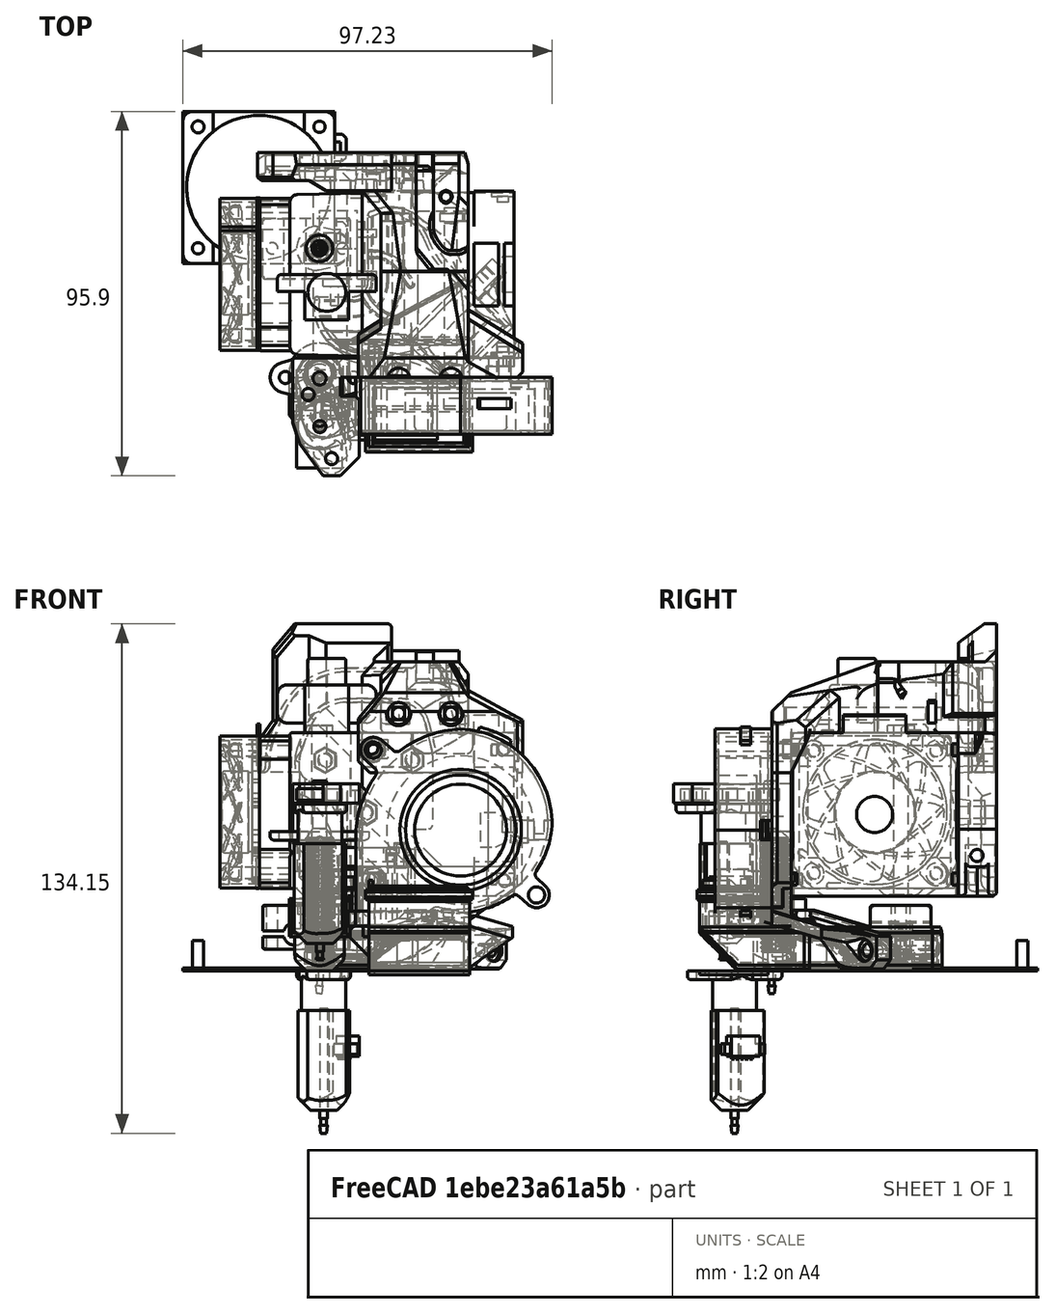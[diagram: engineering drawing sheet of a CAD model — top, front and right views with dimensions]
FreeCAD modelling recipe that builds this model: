
FCSTD DOCUMENT  (FreeCAD 0.18R16146 (Git))
Label: bearmera-5015-rev-1
License: All rights reserved
LicenseURL: http://en.wikipedia.org/wiki/All_rights_reserved
objects: Part::Box×73, Part::Cut×52, Part::Feature×47, Part::MultiFuse×32, Part::Cylinder×31, Part::Chamfer×27, Sketcher::SketchObject×6, PartDesign::Body×4, App::DocumentObjectGroup×3, Part::MultiCommon×3, Mesh::Feature×2, PartDesign::AdditiveLoft×2, PartDesign::Pad×2, App::Part×1
note: 283 computed .brp shape members not serialized (recipe doc carries the construction recipe); baked Part::Feature solids carry a one-line shape summary decoded from their .brp

FEATURE [Part::Feature] Part__Feature018  label="NOZZLE-POS"
  Placement = pos=(-0.025,3.1e-14,12.45) rot=(0.707107,0.707107,0;3.14159rad)
  shape: bbox 8.083 x 7 x 12.5 mm, 18 faces (baked)
FEATURE [Part::Feature] Part__Feature017  label="v6_heaterblock v1"
  Placement = pos=(-14.9885,-8.00025,5.758) rot=(0,0,1;0rad)
  shape: bbox 23 x 16 x 11.5 mm, 37 faces (baked)
FEATURE [Part::Feature] Part__Feature013  label="stepper"
  Placement = pos=(51.225,-28.9,19.7) rot=(0,0,1;1.5708rad)
  shape: bbox 40 x 44 x 47.7 mm, 101 faces (baked)
FEATURE [Part::Feature] Part__Feature014  label="heatsink"
  Placement = pos=(11.225,-28.4,19.7) rot=(0,0,1;1.5708rad)
  shape: bbox 30.92 x 43.26 x 62.61 mm, 110 faces (baked)
FEATURE [Part::Feature] Part__Feature016  label="e3d_hemera_fan v1"
  Placement = pos=(-15.775,13.2,61.8) rot=(0.57735,-0.57735,0.57735;4.18879rad)
  shape: bbox 10.51 x 40.01 x 40.01 mm, 129 faces (baked)
FEATURE [Mesh::Feature] lower_4020_fan_duct  label="lower_4020-fan-duct"
  Placement = pos=(11.3,-33.9,19.8) rot=(0,0,1;0rad)
FEATURE [Part::Feature] Cut007002001001  label="fan-mount-frame001"
  shape: bbox 28.2 x 19.2 x 3.5 mm, 16 faces (baked)
FEATURE [Part::Feature] Part__Feature  label="duct001"
  Placement = pos=(13,-15,0) rot=(0,0,1;0rad)
  shape: bbox 62.87 x 53.67 x 16.75 mm, 145 faces (baked)
FEATURE [Part::Feature] Part__Feature025  label="duct002"
  Placement = pos=(13,-15,0) rot=(0,0,1;0rad)
  shape: bbox 62.87 x 53.67 x 16.75 mm, 145 faces (baked)
FEATURE [Part::Box] Box  label="Cube"
  AttacherType = Attacher::AttachEngine3D
  Height = 17
  Length = 29
  Placement = pos=(26,-38,0) rot=(0,0,1;0rad)
  Width = 48
FEATURE [Part::Box] Box001  label="Cube001"
  AttacherType = Attacher::AttachEngine3D
  Height = 27
  Length = 26
  Placement = pos=(0,-34,0) rot=(0,0,1;0rad)
  Width = 10
FEATURE [Part::Cut] Cut
  Base = -> Part__Feature
  Tool = -> Box
FEATURE [Part::Cut] Cut007002001002
  Base = -> Cut
  Placement = pos=(0,0,-0.45) rot=(0,0,1;0rad)
  Tool = -> Box001
FEATURE [Part::Box] Box002  label="Cube002"
  AttacherType = Attacher::AttachEngine3D
  Height = 2
  Length = 13
  Placement = pos=(13,-24,0.8) rot=(0,0,1;0rad)
  Width = 4
FEATURE [Part::Box] Box003  label="Cube003"
  AttacherType = Attacher::AttachEngine3D
  Height = 1
  Length = 5
  Placement = pos=(21,-24,0.8) rot=(0,0,1;0rad)
  Width = 13
FEATURE [Part::Cut] Cut007002001003
  Base = -> Cut007002001002
  Tool = -> Box002
FEATURE [Part::Cut] Cut007002001004
  Base = -> Cut007002001003
  Tool = -> Box003
FEATURE [Part::Box] Box004  label="Cube004"
  AttacherType = Attacher::AttachEngine3D
  Height = 10
  Length = 24
  Placement = pos=(7,-30,10) rot=(0,0,1;0rad)
  Width = 27
FEATURE [Part::Cut] Cut007002001005
  Base = -> Cut007002001004
  Tool = -> Box004
FEATURE [Part::Box] Box005  label="Cube005"
  AttacherType = Attacher::AttachEngine3D
  Height = 10
  Length = 32
  Placement = pos=(-2,-38,0) rot=(0,0,1;0rad)
  Width = 14
FEATURE [Part::Box] Box007  label="Cube007"
  AttacherType = Attacher::AttachEngine3D
  Height = 10
  Length = 21
  Placement = pos=(26,-24,0) rot=(0,0,1;0rad)
  Width = 21
FEATURE [Part::Box] Box008  label="Cube008"
  AttacherType = Attacher::AttachEngine3D
  Height = 1
  Length = 41
  Placement = pos=(10,-35,9) rot=(0,0,1;0.506145rad)
  Width = 10
FEATURE [Part::MultiFuse] Fusion
  Shapes = -> [Cut007002001005,Box008]
FEATURE [Part::Cut] Cut007002001006
  Base = -> Fusion
  Tool = -> Box005
FEATURE [Part::Cut] Cut007002001007  label="duct-square-cut"
  Base = -> Cut007002001006
  Tool = -> Box007
FEATURE [Part::Feature] Cut007002001007001  label="Cut007002001008"
  Placement = pos=(0,0,1.5) rot=(0,0,1;0rad)
  shape: bbox 41.3 x 51.61 x 10 mm, 88 faces (baked)
FEATURE [Part::Box] Box012  label="Cube012"
  AttacherType = Attacher::AttachEngine3D
  Height = 1
  Length = 26.5
  Placement = pos=(13,-53,0) rot=(0,0,1;0rad)
  Width = 18
FEATURE [Part::Box] Box013  label="Cube013"
  AttacherType = Attacher::AttachEngine3D
  Height = 1
  Length = 23.5
  Placement = pos=(14.5,-51.5,0) rot=(0,0,1;0rad)
  Width = 15
FEATURE [Part::Cut] Cut007002001007002
  Base = -> Box012
  Placement = pos=(0,0,-1) rot=(0,0,1;0rad)
  Tool = -> Box013
FEATURE [Sketcher::SketchObject] Sketch
  AttachmentOffset = pos=(0,0,19) rot=(0,0,1;0rad)
  MapMode = 5
  Placement = pos=(0,0,19) rot=(0,0,1;0rad)
  Support = -> [XY_Plane]
  sketch-geometry (8):
    g0: LineSegment StartX=13 StartY=-35 StartZ=0 EndX=39.5 EndY=-35 EndZ=0
    g1: LineSegment StartX=39.5 StartY=-35 StartZ=0 EndX=39.5 EndY=-53 EndZ=0
    g2: LineSegment StartX=39.5 StartY=-53 StartZ=0 EndX=13 EndY=-53 EndZ=0
    g3: LineSegment StartX=13 StartY=-53 StartZ=0 EndX=13 EndY=-35 EndZ=0
    g4: LineSegment StartX=14.5 StartY=-36.5 StartZ=0 EndX=38 EndY=-36.5 EndZ=0
    g5: LineSegment StartX=38 StartY=-36.5 StartZ=0 EndX=38 EndY=-51.5 EndZ=0
    g6: LineSegment StartX=38 StartY=-51.5 StartZ=0 EndX=14.5 EndY=-51.5 EndZ=0
    g7: LineSegment StartX=14.5 StartY=-51.5 StartZ=0 EndX=14.5 EndY=-36.5 EndZ=0
  constraints (16):
    c: Coincident(g0,g1)
    c: Coincident(g1,g2)
    c: Coincident(g2,g3)
    c: Coincident(g3,g0)
    c: Horizontal(g0)
    c: Horizontal(g2)
    c: Vertical(g1)
    c: Vertical(g3)
    c: Coincident(g4,g5)
    c: Coincident(g5,g6)
    c: Coincident(g6,g7)
    c: Coincident(g7,g4)
    c: Horizontal(g4)
    c: Horizontal(g6)
    c: Vertical(g5)
    c: Vertical(g7)
FEATURE [Sketcher::SketchObject] Sketch001
  AttachmentOffset = pos=(0,0,10.45) rot=(0,0,1;0rad)
  MapMode = 5
  Placement = pos=(0,0,10.45) rot=(0,0,1;0rad)
  Support = -> [XY_Plane]
  sketch-geometry (8):
    g0: LineSegment StartX=13 StartY=-53 StartZ=0 EndX=39.5 EndY=-53 EndZ=0
    g1: LineSegment StartX=39.5 StartY=-53 StartZ=0 EndX=39.5 EndY=-24 EndZ=0
    g2: LineSegment StartX=39.5 StartY=-24 StartZ=0 EndX=13 EndY=-24 EndZ=0
    g3: LineSegment StartX=13 StartY=-24 StartZ=0 EndX=13 EndY=-53 EndZ=0
    g4: LineSegment StartX=38 StartY=-25.5 StartZ=0 EndX=14.5 EndY=-25.5 EndZ=0
    g5: LineSegment StartX=14.5 StartY=-25.5 StartZ=0 EndX=14.5 EndY=-51.5 EndZ=0
    g6: LineSegment StartX=14.5 StartY=-51.5 StartZ=0 EndX=38 EndY=-51.5 EndZ=0
    g7: LineSegment StartX=38 StartY=-51.5 StartZ=0 EndX=38 EndY=-25.5 EndZ=0
  constraints (16):
    c: Coincident(g0,g1)
    c: Coincident(g1,g2)
    c: Coincident(g2,g3)
    c: Coincident(g3,g0)
    c: Horizontal(g0)
    c: Horizontal(g2)
    c: Vertical(g1)
    c: Vertical(g3)
    c: Coincident(g4,g5)
    c: Coincident(g5,g6)
    c: Coincident(g6,g7)
    c: Coincident(g7,g4)
    c: Horizontal(g4)
    c: Horizontal(g6)
    c: Vertical(g5)
    c: Vertical(g7)
FEATURE [PartDesign::AdditiveLoft] AdditiveLoft
  Closed = false
  Profile = -> Sketch
  Ruled = false
  Sections = -> [Sketch001]
FEATURE [PartDesign::Body] Body  label="ramp"
  Group = -> [Sketch,Sketch001,AdditiveLoft]
  Origin = -> Origin
  Tip = -> AdditiveLoft
FEATURE [Part::Feature] Body001  label="ramp001"
  Placement = pos=(0,0,-0.45) rot=(0,0,1;0rad)
  shape: bbox 26.5 x 29 x 8.55 mm, 10 faces (baked)
FEATURE [Sketcher::SketchObject] Sketch002  label="Sketch003"
  AttachmentOffset = pos=(0,0,0.45) rot=(0,0,1;0rad)
  MapMode = 5
  Placement = pos=(0,0,0.45) rot=(0,0,1;0rad)
  Support = -> [XY_Plane001]
  sketch-geometry (8):
    g0: LineSegment StartX=39.5 StartY=-24 StartZ=0 EndX=13 EndY=-24 EndZ=0
    g1: LineSegment StartX=13 StartY=-24 StartZ=0 EndX=13 EndY=-43 EndZ=0
    g2: LineSegment StartX=13 StartY=-43 StartZ=0 EndX=39.5 EndY=-43 EndZ=0
    g3: LineSegment StartX=39.5 StartY=-43 StartZ=0 EndX=39.5 EndY=-24 EndZ=0
    g4: LineSegment StartX=38 StartY=-25.5 StartZ=0 EndX=14.5 EndY=-25.5 EndZ=0
    g5: LineSegment StartX=14.5 StartY=-25.5 StartZ=0 EndX=14.5 EndY=-41.5 EndZ=0
    g6: LineSegment StartX=14.5 StartY=-41.5 StartZ=0 EndX=38 EndY=-41.5 EndZ=0
    g7: LineSegment StartX=38 StartY=-41.5 StartZ=0 EndX=38 EndY=-25.5 EndZ=0
  constraints (16):
    c: Coincident(g0,g1)
    c: Coincident(g1,g2)
    c: Coincident(g2,g3)
    c: Coincident(g3,g0)
    c: Horizontal(g0)
    c: Horizontal(g2)
    c: Vertical(g1)
    c: Vertical(g3)
    c: Coincident(g4,g5)
    c: Coincident(g5,g6)
    c: Coincident(g6,g7)
    c: Coincident(g7,g4)
    c: Horizontal(g4)
    c: Horizontal(g6)
    c: Vertical(g5)
    c: Vertical(g7)
FEATURE [Sketcher::SketchObject] Sketch003  label="Sketch004"
  AttachmentOffset = pos=(0,0,10.45) rot=(0,0,1;0rad)
  MapMode = 5
  Placement = pos=(0,0,10.45) rot=(0,0,1;0rad)
  Support = -> [XY_Plane001]
  sketch-geometry (8):
    g0: LineSegment StartX=13 StartY=-24 StartZ=0 EndX=39.5 EndY=-24 EndZ=0
    g1: LineSegment StartX=39.5 StartY=-24 StartZ=0 EndX=39.5 EndY=-53 EndZ=0
    g2: LineSegment StartX=39.5 StartY=-53 StartZ=0 EndX=13 EndY=-53 EndZ=0
    g3: LineSegment StartX=13 StartY=-53 StartZ=0 EndX=13 EndY=-24 EndZ=0
    g4: LineSegment StartX=14.5 StartY=-25.5 StartZ=0 EndX=38 EndY=-25.5 EndZ=0
    g5: LineSegment StartX=38 StartY=-25.5 StartZ=0 EndX=38 EndY=-51.5 EndZ=0
    g6: LineSegment StartX=38 StartY=-51.5 StartZ=0 EndX=14.5 EndY=-51.5 EndZ=0
    g7: LineSegment StartX=14.5 StartY=-51.5 StartZ=0 EndX=14.5 EndY=-25.5 EndZ=0
  constraints (16):
    c: Coincident(g0,g1)
    c: Coincident(g1,g2)
    c: Coincident(g2,g3)
    c: Coincident(g3,g0)
    c: Horizontal(g0)
    c: Horizontal(g2)
    c: Vertical(g1)
    c: Vertical(g3)
    c: Coincident(g4,g5)
    c: Coincident(g5,g6)
    c: Coincident(g6,g7)
    c: Coincident(g7,g4)
    c: Horizontal(g4)
    c: Horizontal(g6)
    c: Vertical(g5)
    c: Vertical(g7)
FEATURE [PartDesign::AdditiveLoft] AdditiveLoft001
  Closed = false
  Profile = -> Sketch003
  Ruled = false
  Sections = -> [Sketch002]
FEATURE [PartDesign::Body] Body002  label="lower-ramp"
  Group = -> [Sketch002,Sketch003,AdditiveLoft001]
  Origin = -> Origin001
  Tip = -> AdditiveLoft001
FEATURE [Part::Feature] Body002002  label="lower-ramp002"
  Placement = pos=(0,0,-0.45) rot=(0,0,1;0rad)
  shape: bbox 26.5 x 29 x 10 mm, 10 faces (baked)
FEATURE [Sketcher::SketchObject] Sketch004  label="Sketch005"
  MapMode = 5
  Support = -> [XY_Plane002]
  sketch-geometry (31):
    g0: GeomPoint X=26 Y=-24 Z=0
    g1: LineSegment StartX=26 StartY=-24 StartZ=0 EndX=1.71 EndY=-24 EndZ=0
    g2: LineSegment StartX=26 StartY=-24 StartZ=0 EndX=26 EndY=8.3 EndZ=0
    g3: LineSegment StartX=13 StartY=-31 StartZ=0 EndX=14.5 EndY=-31 EndZ=0
    g4: LineSegment StartX=14.5 StartY=-31 StartZ=0 EndX=14.5 EndY=-25.5 EndZ=0
    g5: LineSegment StartX=14.5 StartY=-25.5 StartZ=0 EndX=39.5 EndY=-25.5 EndZ=0
    g6: LineSegment StartX=39.5 StartY=-25.5 StartZ=0 EndX=39.5 EndY=-24 EndZ=0
    g7-g12: Circle [constr] x6 (B-spline internal-alignment scaffolding for g13; pole/knot coordinates omitted)
    g13: BSplineCurve PolesCount=6 KnotsCount=4 Degree=3 IsPeriodic=0
    g14-g17: GeomPoint [constr] x4 (B-spline internal-alignment scaffolding for g13; pole/knot coordinates omitted)
    g18-g24: Circle [constr] x7 (B-spline internal-alignment scaffolding for g25; pole/knot coordinates omitted)
    g25: BSplineCurve PolesCount=7 KnotsCount=5 Degree=3 IsPeriodic=0
    g26-g30: GeomPoint [constr] x5 (B-spline internal-alignment scaffolding for g25; pole/knot coordinates omitted)
  constraints (24):
    c: DistanceY(g0,g-1) = 24
    c: DistanceX(g-1,g0) = 26
    c: Coincident(g1,g0)
    c: Horizontal(g1)
    c: Coincident(g2,g0)
    c: Vertical(g2)
    c: Coincident(g3,g4)
    c: Vertical(g4)
    c: Coincident(g4,g5)
    c: Horizontal(g5)
    c: Coincident(g5,g6)
    c: DistanceY(g2,g2) = 32.3
    c: Coincident(g13,g1)
    c: Radius(g7) = 0.6
    c: Equal(g7, g8-g12) x5
    c: Coincident(g13,g3)
    c: InternalAlignment(g7-g12 -> g13) x6
    c: InternalAlignment(g14-g17 -> g13) x4
    c: Coincident(g25,g2)
    c: Radius(g18) = 1
    c: Equal(g18, g19-g24) x6
    c: Coincident(g25,g6)
    c: InternalAlignment(g18-g24 -> g25) x7
    c: InternalAlignment(g26-g30 -> g25) x5
FEATURE [PartDesign::Pad] Pad
  Length = 10
  Length2 = 100
  Profile = -> Sketch004
  Type = 0
FEATURE [PartDesign::Body] Body002003  label="outer"
  Group = -> [Sketch004,Pad]
  Origin = -> Origin002
  Tip = -> Pad
FEATURE [Sketcher::SketchObject] Sketch005  label="Sketch006"
  MapMode = 5
  Support = -> [XY_Plane003]
  sketch-geometry (29):
    g0: GeomPoint X=26 Y=-24 Z=0
    g1: LineSegment StartX=26 StartY=-24 StartZ=0 EndX=3.42 EndY=-24 EndZ=0
    g2: LineSegment StartX=26 StartY=-24 StartZ=0 EndX=26 EndY=6.6 EndZ=0
    g3: GeomPoint X=14.5 Y=-30 Z=0
    g4: GeomPoint X=38 Y=-25.5 Z=0
    g5-g10: Circle [constr] x6 (B-spline internal-alignment scaffolding for g11; pole/knot coordinates omitted)
    g11: BSplineCurve PolesCount=6 KnotsCount=4 Degree=3 IsPeriodic=0
    g12-g15: GeomPoint [constr] x4 (B-spline internal-alignment scaffolding for g11; pole/knot coordinates omitted)
    g16-g21: Circle [constr] x6 (B-spline internal-alignment scaffolding for g22; pole/knot coordinates omitted)
    g22: BSplineCurve PolesCount=6 KnotsCount=4 Degree=3 IsPeriodic=0
    g23-g26: GeomPoint [constr] x4 (B-spline internal-alignment scaffolding for g22; pole/knot coordinates omitted)
    g27: LineSegment StartX=14.5 StartY=-30 StartZ=0 EndX=14.5 EndY=-25.5 EndZ=0
    g28: LineSegment StartX=14.5 StartY=-25.5 StartZ=0 EndX=38 EndY=-25.5 EndZ=0
  constraints (29):
    c: DistanceY(g0,g-1) = 24
    c: DistanceX(g-1,g0) = 26
    c: Coincident(g1,g0)
    c: Horizontal(g1)
    c: Coincident(g2,g0)
    c: Vertical(g2)
    c: DistanceY(g2,g2) = 30.6
    c: DistanceX(g1,g1) = 22.58
    c: DistanceY(g4,g-1) = 25.5
    c: DistanceX(g-1,g4) = 38
    c: DistanceY(g3,g-1) = 30
    c: DistanceX(g-1,g3) = 14.5
    c: Coincident(g11,g1)
    c: Radius(g5) = 0.4
    c: Equal(g5, g6-g10) x5
    c: Coincident(g11,g3)
    c: InternalAlignment(g5-g10 -> g11) x6
    c: InternalAlignment(g12-g15 -> g11) x4
    c: Coincident(g22,g2)
    c: Radius(g16) = 1
    c: Equal(g16, g17-g21) x5
    c: Coincident(g22,g4)
    c: InternalAlignment(g16-g21 -> g22) x6
    c: InternalAlignment(g23-g26 -> g22) x4
    c: Coincident(g27,g3)
    c: Vertical(g27)
    c: Coincident(g28,g27)
    c: Coincident(g28,g4)
    c: Horizontal(g28)
FEATURE [PartDesign::Pad] Pad001
  Length = 8.2
  Length2 = 100
  Profile = -> Sketch005
  Type = 0
FEATURE [PartDesign::Body] Body002004  label="inner"
  Group = -> [Sketch005,Pad001]
  Origin = -> Origin003
  Tip = -> Pad001
FEATURE [App::DocumentObjectGroup] Group001  label="Sketch002"
  Group = -> [Body,Body002,Body002003,Body002004]
FEATURE [Part::Box] Box015  label="Cube015"
  AttacherType = Attacher::AttachEngine3D
  Height = 8.2
  Length = 23.5
  Placement = pos=(14.5,-27,0.8) rot=(0,0,1;0rad)
  Width = 5
FEATURE [Part::Box] Box016  label="Cube016"
  AttacherType = Attacher::AttachEngine3D
  Height = 0.8
  Length = 23.5
  Placement = pos=(14.5,-42.5,0) rot=(0,0,1;0rad)
  Width = 18
FEATURE [Part::Feature] Body002004002  label="inner002"
  Placement = pos=(0,0,0.8) rot=(0,0,1;0rad)
  shape: bbox 34.69 x 36.6 x 8.2 mm, 8 faces (baked)
FEATURE [Part::Feature] Cut007002001007009  label="fan-mount-frame002"
  Placement = pos=(0,0,-0.45) rot=(0,0,1;0rad)
  shape: bbox 28.2 x 19.2 x 3.5 mm, 16 faces (baked)
FEATURE [Part::MultiFuse] Fusion001
  Shapes = -> [Box016,Body002002]
FEATURE [Part::Cut] Cut007002001007011
  Base = -> Fusion001
  Tool = -> Box015
FEATURE [Part::Box] Box018  label="Cube018"
  AttacherType = Attacher::AttachEngine3D
  Height = 1
  Length = 36.5
  Placement = pos=(5.64694,-26.4947,8.5) rot=(0,0,1;0.488692rad)
  Width = 1
FEATURE [Part::Chamfer] Chamfer005
  Base = -> Box018
  Edges = 1 edges r=0.5: [Edge9]
  Placement = pos=(0,0,1) rot=(0,0,1;0rad)
FEATURE [Part::Cylinder] Cylinder001  label="stepper-screw-pos"
  Angle = 360
  AttacherType = Attacher::AttachEngine3D
  Height = 10
  Placement = pos=(48.73,-25,58.7) rot=(1,0,0;1.5708rad)
  Radius = 1.65
FEATURE [Part::Cylinder] Cylinder002  label="fill"
  Angle = 360
  AttacherType = Attacher::AttachEngine3D
  Height = 5
  Placement = pos=(48.23,-28.9,58.2) rot=(1,0,0;1.5708rad)
  Radius = 3
FEATURE [Part::Cylinder] Cylinder003  label="fill001"
  Angle = 360
  AttacherType = Attacher::AttachEngine3D
  Height = 5
  Placement = pos=(14.23,-28.9,58.2) rot=(1,0,0;1.5708rad)
  Radius = 3
FEATURE [Part::Box] Box020  label="Cube020"
  AttacherType = Attacher::AttachEngine3D
  Height = 4
  Length = 4
  Placement = pos=(10,-28.9,56) rot=(0,0,1;0rad)
  Width = 3
FEATURE [Part::Box] Box021  label="Cube021"
  AttacherType = Attacher::AttachEngine3D
  Height = 6
  Length = 4
  Placement = pos=(48.55,-28.9,55.2) rot=(0,0,1;0rad)
  Width = 5
FEATURE [Part::Cylinder] Cylinder004  label="stepper-screw-pos001"
  Angle = 360
  AttacherType = Attacher::AttachEngine3D
  Height = 10
  Placement = pos=(13.73,-25,58.7) rot=(1,0,0;1.5708rad)
  Radius = 1.65
FEATURE [Part::Cylinder] Cylinder005  label="stepper-screw-pos002"
  Angle = 360
  AttacherType = Attacher::AttachEngine3D
  Height = 10
  Placement = pos=(48.23,-25,58.2) rot=(1,0,0;1.5708rad)
  Radius = 1.6
FEATURE [Part::Cylinder] Cylinder006  label="stepper-screw-pos003"
  Angle = 360
  AttacherType = Attacher::AttachEngine3D
  Height = 10
  Placement = pos=(13.73,-25,25.1) rot=(1,0,0;1.5708rad)
  Radius = 0.5
FEATURE [Part::Cylinder] Cylinder007  label="stepper-screw-pos004"
  Angle = 360
  AttacherType = Attacher::AttachEngine3D
  Height = 10
  Placement = pos=(48.73,-25,23.7) rot=(1,0,0;1.5708rad)
  Radius = 1.6
FEATURE [Part::Feature] Part__Feature012001  label="body_front001"
  Placement = pos=(-5.275,25.1,21) rot=(0,0,-1;1.5708rad)
  shape: bbox 44.13 x 28.92 x 79.97 mm, 174 faces (baked)
FEATURE [Part::Feature] Part__Feature012002  label="body_front002"
  Placement = pos=(-5.275,25.1,21) rot=(0,0,-1;1.5708rad)
  shape: bbox 44.13 x 28.92 x 79.97 mm, 174 faces (baked)
FEATURE [Part::MultiFuse] Fusion008
  Shapes = -> [Part__Feature012002,Cylinder003]
FEATURE [Part::MultiFuse] Fusion009
  Shapes = -> [Fusion008,Cylinder002]
FEATURE [Part::Cut] Cut007002001007014
  Base = -> Fusion009
  Tool = -> Box020
FEATURE [Part::Cut] Cut007002001007015
  Base = -> Cut007002001007014
  Tool = -> Box021
FEATURE [Part::Cut] Cut007002001007016
  Base = -> Cut007002001007015
  Tool = -> Cylinder001
FEATURE [Part::Cut] Cut007002001007017
  Base = -> Cut007002001007016
  Tool = -> Cylinder004
FEATURE [Part::Box] Box022  label="Cube022"
  AttacherType = Attacher::AttachEngine3D
  Height = 5
  Length = 7
  Placement = pos=(11,-31,56) rot=(0,0,1;0rad)
  Width = 10
FEATURE [Part::MultiCommon] Common  label="body-pos-fix"
  Shapes = -> [Box022,Part__Feature012001]
FEATURE [Part::Feature] Common001  label="body-pos-fix001"
  Placement = pos=(0,0,-34) rot=(0,0,1;0rad)
  shape: bbox 7 x 3.1 x 5 mm, 23 faces (baked)
FEATURE [Part::Box] Box023  label="Cube023"
  AttacherType = Attacher::AttachEngine3D
  Height = 10
  Length = 10
  Placement = pos=(4,-28.9,19) rot=(0,0,1;0rad)
  Width = 10
FEATURE [Part::Cut] Cut007002001007018
  Base = -> Common001
  Tool = -> Box023
FEATURE [Part::Cylinder] Cylinder008  label="tmpp"
  Angle = 360
  AttacherType = Attacher::AttachEngine3D
  Height = 2.1
  Placement = pos=(14.23,-28.9,24.2) rot=(1,0,0;1.5708rad)
  Radius = 1.7
FEATURE [Part::MultiFuse] Fusion010  label="body-pos-2"
  Shapes = -> [Cylinder008,Cut007002001007018]
FEATURE [Part::Box] Box024  label="Cube024"
  AttacherType = Attacher::AttachEngine3D
  Height = 14
  Length = 41
  Placement = pos=(10.23,-33.9,13.5) rot=(0,0,1;0rad)
  Width = 5
FEATURE [Part::Cylinder] Cylinder009  label="stepper-screw-pos005"
  Angle = 360
  AttacherType = Attacher::AttachEngine3D
  Height = 12
  Placement = pos=(13.73,-31,26.4) rot=(1,0,0;1.5708rad)
  Radius = 0.5
FEATURE [Part::Feature] Fusion010002  label="body-pos-1"
  Placement = pos=(62.4,0,48.4) rot=(0,1,0;3.14159rad)
  shape: bbox 7 x 3.1 x 5 mm, 25 faces (baked)
FEATURE [Part::Box] Box026  label="Cube026"
  AttacherType = Attacher::AttachEngine3D
  Height = 10
  Length = 30
  Placement = pos=(40.8236,-35.5,2.21194) rot=(0,-1,0;0.610865rad)
  Width = 10
FEATURE [Part::Box] Box027  label="Cube027"
  AttacherType = Attacher::AttachEngine3D
  Height = 10
  Length = 10
  Placement = pos=(51.23,-38,19) rot=(0,0,1;0rad)
  Width = 10
FEATURE [Part::Box] Box028  label="Cube028"
  AttacherType = Attacher::AttachEngine3D
  Height = 29
  Length = 10
  Placement = pos=(44,-41,0) rot=(0,0,1;0rad)
  Width = 10
FEATURE [Part::Cylinder] Cylinder010  label="stepper-screw-pos006"
  Angle = 360
  AttacherType = Attacher::AttachEngine3D
  Height = 10
  Placement = pos=(48.73,-25,25.1) rot=(1,0,0;1.5708rad)
  Radius = 0.5
FEATURE [Part::Cylinder] Cylinder011  label="stepper-screw-pos007"
  Angle = 360
  AttacherType = Attacher::AttachEngine3D
  Height = 10
  Placement = pos=(48.73,-25,23.7) rot=(1,0,0;1.5708rad)
  Radius = 1.6
FEATURE [Part::Cylinder] Cylinder012  label="stepper-screw-pos008"
  Angle = 360
  AttacherType = Attacher::AttachEngine3D
  Height = 12
  Placement = pos=(13.73,-31,23.7) rot=(1,0,0;1.5708rad)
  Radius = 3
FEATURE [Part::Cylinder] Cylinder013  label="stepper-screw-pos009"
  Angle = 360
  AttacherType = Attacher::AttachEngine3D
  Height = 10
  Placement = pos=(13.73,-25,23.7) rot=(1,0,0;1.5708rad)
  Radius = 1.6
FEATURE [Part::Box] Box029  label="Cube029"
  AttacherType = Attacher::AttachEngine3D
  Height = 10
  Length = 10
  Placement = pos=(9,-29,13.8) rot=(0,0,1;0rad)
  Width = 10
FEATURE [Part::Chamfer] Chamfer009
  Base = -> Box029
  Edges = 1 edges r=2: [Edge10]
  Placement = pos=(0,0.1,1) rot=(0,0,1;0rad)
FEATURE [Part::Feature] Chamfer009001  label="Chamfer010"
  Placement = pos=(32,0.1,1) rot=(0,0,1;0rad)
  shape: bbox 10 x 10 x 10 mm, 7 faces (baked)
FEATURE [Part::Box] Box030  label="Cube030"
  AttacherType = Attacher::AttachEngine3D
  Height = 60
  Length = 63
  Placement = pos=(0,-43.2,-7.8) rot=(0,0,1;0rad)
  Width = 30
FEATURE [Part::Cut] Cut007002001007029003002  label="tmp-body-front"
  Base = -> Cut007002001007017
  Tool = -> Box030
FEATURE [Part::Feature] Part__Feature011  label="body_back"
  Placement = pos=(-5.275,25.2,21) rot=(0,0,-1;1.5708rad)
  shape: bbox 55.53 x 31.22 x 71.72 mm, 411 faces (baked)
FEATURE [Part::Feature] Part__Feature020  label="pinda v4_y33"
  Placement = pos=(0.025,-33,5) rot=(0,0,-1;1.5708rad)
  shape: bbox 9.315 x 9.314 x 49.01 mm, 71 faces (baked)
FEATURE [Part::Feature] Box025001  label="Cube031"
  Placement = pos=(0,0,1.5) rot=(0,0,1;0rad)
  shape: bbox 23.5 x 14.03 x 14.03 mm, 6 faces (baked)
FEATURE [Part::MultiFuse] Fusion010008
  Shapes = -> [Cylinder007,Cylinder010]
FEATURE [Part::MultiFuse] Fusion010009
  Shapes = -> [Cylinder013,Cylinder006]
FEATURE [Part::MultiFuse] Fusion010010
  Shapes = -> [Cylinder012,Cylinder009]
FEATURE [Part::Cut] Cut007002001007029003013
  Base = -> Box024
  Tool = -> Box025001
FEATURE [Part::Cut] Cut007002001007029003014
  Base = -> Fusion010
  Tool = -> Chamfer009
FEATURE [Part::Cut] Cut007002001007029003015
  Base = -> Fusion010002
  Tool = -> Chamfer009001
FEATURE [Part::MultiFuse] Fusion010014
  Shapes = -> [Cut007002001007029003013,Cut007002001007029003015]
FEATURE [Part::MultiFuse] Fusion010015
  Shapes = -> [Fusion010014,Cut007002001007029003014]
FEATURE [Part::Cut] Cut007002001007029003016
  Base = -> Fusion010015
  Tool = -> Box027
FEATURE [Part::Cut] Cut007002001007029003017
  Base = -> Cut007002001007029003016
  Tool = -> Box028
FEATURE [Part::Cut] Cut007002001007029003018
  Base = -> Cut007002001007029003017
  Tool = -> Fusion010008
FEATURE [Part::Cut] Cut007002001007029003019
  Base = -> Cut007002001007029003018
  Tool = -> Fusion010009
FEATURE [Part::Cut] Cut007002001007029003020
  Base = -> Cut007002001007029003019
  Tool = -> Fusion010010
FEATURE [Part::Cut] Cut007002001007029003021
  Base = -> Cut007002001007029003020
  Tool = -> Box026
FEATURE [Part::Chamfer] Chamfer009002
  Base = -> Cut007002001007009
  Edges = 1 edges r=0.8: [Edge12]
FEATURE [Part::Chamfer] Chamfer009003
  Base = -> Chamfer009002
  Edges = 1 edges r=0.6: [Edge1]
FEATURE [Part::Chamfer] Chamfer009004
  Base = -> Chamfer009003
  Edges = 1 edges r=0.9: [Edge15]
FEATURE [Part::Chamfer] Chamfer009006
  Base = -> Cut007002001007029003021
  Edges = 1 edges r=3: [Edge4]
FEATURE [Part::Chamfer] Chamfer009007  label="fan-mount-plate"
  Base = -> Chamfer009006
  Edges = 2 edges r=1: [Edge3,Edge20]
FEATURE [Part::Cylinder] Cylinder
  Angle = 360
  AttacherType = Attacher::AttachEngine3D
  Height = 10
  Radius = 1.6
FEATURE [Part::Cylinder] Cylinder015
  Angle = 360
  AttacherType = Attacher::AttachEngine3D
  Height = 8
  Placement = pos=(0,32,0) rot=(0,0,1;0rad)
  Radius = 1.5
FEATURE [Part::Cylinder] Cylinder016
  Angle = 360
  AttacherType = Attacher::AttachEngine3D
  Height = 8
  Placement = pos=(-32,0,0) rot=(0,0,1;0rad)
  Radius = 1.5
FEATURE [Part::Cylinder] Cylinder017
  Angle = 360
  AttacherType = Attacher::AttachEngine3D
  Height = 10
  Placement = pos=(-32,32,0) rot=(0,0,1;0rad)
  Radius = 1.6
FEATURE [Part::Cylinder] Cylinder018
  Angle = 360
  AttacherType = Attacher::AttachEngine3D
  Height = 10
  Placement = pos=(-16,16,0) rot=(0,0,1;0rad)
  Radius = 19
FEATURE [Part::Box] Box025003  label="Cube033"
  AttacherType = Attacher::AttachEngine3D
  Height = 0.7
  Length = 40
  Placement = pos=(-36,-4,0) rot=(0,0,1;0rad)
  Width = 40
FEATURE [Part::Cut] Cut007002001007029003024
  Base = -> Box025003
  Tool = -> Cylinder017
FEATURE [Part::Cut] Cut007002001007029003025
  Base = -> Cut007002001007029003024
  Tool = -> Cylinder
FEATURE [Part::Cut] Cut007002001007029003026
  Base = -> Cut007002001007029003025
  Tool = -> Cylinder018
FEATURE [Part::Feature] Fillet001
  shape: bbox 40 x 40 x 0.7 mm, 13 faces (baked)
FEATURE [Part::Feature] Fillet002
  shape: bbox 40 x 40 x 0.7 mm, 13 faces (baked)
FEATURE [Part::Box] Box025004  label="Cube034"
  AttacherType = Attacher::AttachEngine3D
  Height = 10
  Length = 8
  Placement = pos=(-4,-4,0) rot=(0,0,1;0rad)
  Width = 40
FEATURE [Part::Box] Box025005  label="Cube035"
  AttacherType = Attacher::AttachEngine3D
  Height = 10
  Length = 8
  Placement = pos=(-36,-4,0) rot=(0,0,1;0rad)
  Width = 40
FEATURE [Part::MultiCommon] Common002  label="fan-spacer-lower-tmp"
  Shapes = -> [Box025005,Fillet001]
FEATURE [Part::MultiCommon] Common003
  Shapes = -> [Fillet002,Box025004]
FEATURE [Part::Box] Box025006  label="Cube036"
  AttacherType = Attacher::AttachEngine3D
  Height = 0.7
  Length = 3
  Placement = pos=(4,0,0) rot=(0,0,1;0rad)
  Width = 7
FEATURE [Part::Box] Box025007  label="Cube037"
  AttacherType = Attacher::AttachEngine3D
  Height = 0.7
  Length = 1.5
  Placement = pos=(4,2,0) rot=(0,0,1;0rad)
  Width = 3
FEATURE [Part::MultiFuse] Fusion010020005  label="fan-spacer-lower"
  Shapes = -> [Common002,Cylinder016]
FEATURE [Part::Cut] Cut007002001007029003027
  Base = -> Box025006
  Tool = -> Box025007
FEATURE [Part::Chamfer] Chamfer009008
  Base = -> Cut007002001007029003027
  Edges = 2 edges r=1: [Edge20,Edge24]
FEATURE [Part::Feature] Chamfer009008001  label="Chamfer009009"
  Placement = pos=(0,23,0) rot=(0,0,1;0rad)
  shape: bbox 3 x 7 x 0.7 mm, 12 faces (baked)
FEATURE [Part::MultiFuse] Fusion010020006  label="fan-spacer-upper"
  Shapes = -> [Common003,Chamfer009008,Chamfer009008001,Cylinder015]
FEATURE [App::DocumentObjectGroup] Group002  label="export"
  Group = -> [Fusion010020006,Fusion010020005]
FEATURE [Mesh::Feature] turbo_fan_35x18_2_  label="4020-fan"
  Placement = pos=(31.25,-53.5,41.25) rot=(1,0,0;1.5708rad)
FEATURE [Part::Feature] Cut007002001002005001  label="fan-mount-frame-lower"
  Placement = pos=(11.7,-54,18.85) rot=(0,0,1;0rad)
  shape: bbox 28.2 x 19.2 x 3.5 mm, 16 faces (baked)
FEATURE [Part::Feature] Fusion010020005001  label="fan-spacer-lower001"
  Placement = pos=(-16,-22.75,57.75) rot=(0,-1,0;1.5708rad)
  shape: bbox 8 x 40 x 8 mm, 13 faces (baked)
FEATURE [Part::Feature] Fusion010020006001  label="fan-spacer-upper001"
  Placement = pos=(-15.7,-22.75,58) rot=(0,-1,0;1.5708rad)
  shape: bbox 8 x 40 x 11 mm, 33 faces (baked)
FEATURE [Part::Box] Box025013  label="Cube043"
  AttacherType = Attacher::AttachEngine3D
  Height = 36
  Length = 9
  Placement = pos=(44.45,-33.9,16.64) rot=(0,0,1;0rad)
  Width = 5
FEATURE [Part::Chamfer] Chamfer009008010
  Base = -> Box025013
  Edges = 1 edges r=1.3: [Edge5]
FEATURE [Part::Cut] Cut007002001007029003034
  Base = -> Chamfer009008010
  Tool = -> Cylinder011
FEATURE [Part::Feature] Box025014001  label="Cube045"
  Placement = pos=(-6.4,0,14.95) rot=(0,0,1;0rad)
  shape: bbox 24.82 x 24 x 25.31 mm, 6 faces (baked)
FEATURE [Part::Cut] Cut007002001007029003035
  Base = -> Cut007002001007029003034
  Tool = -> Box025014001
FEATURE [Part::Box] Box025014002  label="Cube046"
  AttacherType = Attacher::AttachEngine3D
  Height = 12
  Length = 8
  Placement = pos=(43.3,-31.1,15.6) rot=(0,0,1;0rad)
  Width = 3
FEATURE [Part::Cut] Cut007002001007029003036
  Base = -> Cut007002001007029003035
  Tool = -> Box025014002
FEATURE [Part::MultiFuse] Fusion010020009002  label="front-rev-1"
  Shapes = -> [Cut007002001007029003002,Cut007002001007029003036]
FEATURE [Part::Cylinder] Cylinder019
  Angle = 360
  AttacherType = Attacher::AttachEngine3D
  Height = 10
  Placement = pos=(0,-33,10) rot=(0,0,1;0rad)
  Radius = 8
FEATURE [Part::Cylinder] Cylinder020
  Angle = 360
  AttacherType = Attacher::AttachEngine3D
  Height = 10
  Placement = pos=(0,-33,9) rot=(0,0,1;0rad)
  Radius = 4
FEATURE [Part::Box] Box025014003  label="Cube047"
  AttacherType = Attacher::AttachEngine3D
  Height = 10
  Length = 16
  Placement = pos=(-8,-45,10) rot=(0,0,1;0rad)
  Width = 12
FEATURE [Part::Box] Box025014004  label="Cube048"
  AttacherType = Attacher::AttachEngine3D
  Height = 11
  Length = 1.5
  Placement = pos=(-1,-46,9) rot=(0,0,1;0rad)
  Width = 12
FEATURE [Part::MultiFuse] Fusion010020009003
  Placement = pos=(0,0,-1) rot=(0,0,1;0rad)
  Shapes = -> [Box025014003,Cylinder019]
FEATURE [Part::Cylinder] Cylinder021
  Angle = 360
  AttacherType = Attacher::AttachEngine3D
  Height = 20
  Placement = pos=(11,-40,15) rot=(0,-1,0;1.5708rad)
  Radius = 1.6
FEATURE [Part::Cylinder] Cylinder022
  Angle = 360
  AttacherType = Attacher::AttachEngine3D
  Height = 3
  Placement = pos=(-5,-40,17.8) rot=(0,-1,0;1.5708rad)
  Radius = 0.5
FEATURE [Part::Cylinder] Cylinder023
  Angle = 360
  AttacherType = Attacher::AttachEngine3D
  Height = 20
  Placement = pos=(11,-40,16.4) rot=(0,-1,0;1.5708rad)
  Radius = 0.5
FEATURE [Part::Cylinder] Cylinder024
  Angle = 360
  AttacherType = Attacher::AttachEngine3D
  Height = 3
  Placement = pos=(-5,-40,15) rot=(0,-1,0;1.5708rad)
  Radius = 3
FEATURE [Part::Box] Box025014010  label="Cube054"
  AttacherType = Attacher::AttachEngine3D
  Height = 6
  Length = 2
  Placement = pos=(3,-46,11) rot=(0,0,1;0rad)
  Width = 9
FEATURE [Part::MultiFuse] Fusion010020009004
  Placement = pos=(0,0,-1) rot=(0,0,1;0rad)
  Shapes = -> [Cylinder024,Cylinder022]
FEATURE [Part::MultiFuse] Fusion010020009005
  Placement = pos=(0,0,-1) rot=(0,0,1;0rad)
  Shapes = -> [Cylinder021,Cylinder023]
FEATURE [Part::Box] Box025014011  label="probe-mount-pos-arm"
  AttacherType = Attacher::AttachEngine3D
  Height = 6
  Length = 6
  Placement = pos=(5.23,-32.4,15) rot=(0,0,1;0rad)
  Width = 2
FEATURE [Part::Box] Box025014013  label="Cube055"
  AttacherType = Attacher::AttachEngine3D
  Height = 19
  Length = 5
  Placement = pos=(5.23,-33.9,9) rot=(0,0,1;0rad)
  Width = 5
FEATURE [Part::Chamfer] Chamfer009008018
  Base = -> Box025014011
  Edges = 2 edges r=1: [Edge6,Edge8]
FEATURE [Part::Box] Box025014014  label="Cube056"
  AttacherType = Attacher::AttachEngine3D
  Height = 5
  Length = 18
  Placement = pos=(5.23,-33.9,27.5) rot=(0,0,1;0rad)
  Width = 5
FEATURE [Part::Cylinder] Cylinder026
  Angle = 360
  AttacherType = Attacher::AttachEngine3D
  Height = 14
  Placement = pos=(19,-31.4,25) rot=(0,0,1;0rad)
  Radius = 1
FEATURE [Part::Cylinder] Cylinder027
  Angle = 360
  AttacherType = Attacher::AttachEngine3D
  Height = 2
  Placement = pos=(19,-31.4,31) rot=(0,0,1;0rad)
  Radius = 2
FEATURE [Part::Chamfer] Chamfer009008024
  Base = -> Box025014013
  Edges = 1 edges r=4: [Edge8]
FEATURE [Part::Feature] Cut007002001007029003046001  label="fan-duct-rev-2-refined"
  shape: bbox 52.67 x 64.46 x 26 mm, 198 faces (baked)
FEATURE [Part::Cut] Cut007002001007029003046002
  Base = -> Box025014014
  Tool = -> Cylinder026
FEATURE [Part::Chamfer] Chamfer009008025
  Base = -> Cut007002001007029003046002
  Edges = 1 edges r=1.5: [Edge9]
FEATURE [Part::Chamfer] Chamfer009008026
  Base = -> Chamfer009008025
  Edges = 1 edges r=2: [Edge15]
FEATURE [Part::Cut] Cut007002001007029003046003
  Base = -> Chamfer009008026
  Tool = -> Cylinder027
FEATURE [Part::MultiFuse] Fusion010020009006
  Shapes = -> [Chamfer009008024,Chamfer009008018,Cut007002001007029003046003]
FEATURE [Part::Chamfer] Chamfer009008027
  Base = -> Fusion010020009006
  Edges = 2 edges r=1: [Edge11,Edge19]
FEATURE [Part::Box] Box025014015  label="Cube057"
  AttacherType = Attacher::AttachEngine3D
  Height = 18.3
  Length = 1.7
  Placement = pos=(11.53,-33.9,9) rot=(0,0,1;0rad)
  Width = 5
FEATURE [Part::Feature] Fusion010020009002001  label="front-rev-1-refined"
  shape: bbox 43.24 x 28.92 x 64.47 mm, 118 faces (baked)
FEATURE [Part::Box] Box025014016  label="Cube058"
  AttacherType = Attacher::AttachEngine3D
  Height = 2.8
  Length = 5
  Placement = pos=(10,3,1.5) rot=(0,0,1;0rad)
  Width = 2
FEATURE [Part::Box] Box025014017  label="Cube059"
  AttacherType = Attacher::AttachEngine3D
  Height = 2.8
  Length = 5
  Placement = pos=(10,-8,1.5) rot=(0,0,1;0rad)
  Width = 2
FEATURE [Part::Box] Box025014018  label="Cube060"
  AttacherType = Attacher::AttachEngine3D
  Height = 2.8
  Length = 2
  Placement = pos=(3,-15,1.5) rot=(0,0,1;0rad)
  Width = 5
FEATURE [Part::Box] Box025014019  label="Cube061"
  AttacherType = Attacher::AttachEngine3D
  Height = 1
  Length = 2
  Placement = pos=(10,-10,1.5) rot=(0,0,1;0rad)
  Width = 17
FEATURE [Part::Box] Box025014020  label="Cube062"
  AttacherType = Attacher::AttachEngine3D
  Height = 1
  Length = 10
  Placement = pos=(1,-10,1.5) rot=(0,0,1;0rad)
  Width = 2
FEATURE [Part::MultiFuse] Fusion010020009007003  label="fan-support"
  Shapes = -> [Box025014016,Box025014019,Box025014017,Box025014020,Box025014018]
FEATURE [Part::MultiFuse] Fusion010020009007004  label="fan-w-support"
  Shapes = -> [Cut007002001007029003046001,Fusion010020009007003]
FEATURE [Part::MultiFuse] Fusion010020009007005
  Shapes = -> [Fusion010020009004,Fusion010020009005]
FEATURE [Part::Cut] Cut007002001007029003046004
  Base = -> Fusion010020009003
  Tool = -> Cylinder020
FEATURE [Part::Cut] Cut007002001007029003046005
  Base = -> Cut007002001007029003046004
  Tool = -> Fusion010020009007005
FEATURE [Part::Chamfer] Chamfer009008028
  Base = -> Cut007002001007029003046005
  Edges = 4 edges r=1: [Edge1,Edge8,Edge9,Edge10]
FEATURE [Part::Box] Box025014021  label="Cube063"
  AttacherType = Attacher::AttachEngine3D
  Height = 18.3
  Length = 1.7
  Placement = pos=(14.53,-33.9,9) rot=(0,0,1;0rad)
  Width = 5
FEATURE [Part::Box] Box025014022  label="Cube064"
  AttacherType = Attacher::AttachEngine3D
  Height = 18.3
  Length = 1.7
  Placement = pos=(17.53,-33.9,9) rot=(0,0,1;0rad)
  Width = 5
FEATURE [Part::Box] Box025014023  label="Cube065"
  AttacherType = Attacher::AttachEngine3D
  Height = 18.3
  Length = 2.7
  Placement = pos=(20.53,-33.9,9) rot=(0,0,1;0rad)
  Width = 5
FEATURE [Part::MultiFuse] Fusion010020009007006002  label="probe-custom-support"
  Shapes = -> [Box025014015,Box025014021,Box025014022,Box025014023]
FEATURE [Part::Cylinder] Cylinder028
  Angle = 360
  AttacherType = Attacher::AttachEngine3D
  Height = 19
  Placement = pos=(0,-33,0) rot=(0,0,1;0rad)
  Radius = 4.05
FEATURE [Part::Cut] Cut007002001007029003046006
  Base = -> Chamfer009008028
  Tool = -> Cylinder028
FEATURE [Part::Cut] Cut007002001007029003046007
  Base = -> Cut007002001007029003046006
  Tool = -> Box025014004
FEATURE [Part::Cut] Cut007002001007029003046008
  Base = -> Cut007002001007029003046007
  Tool = -> Box025014010
FEATURE [Part::Chamfer] Chamfer009008029
  Base = -> Cut007002001007029003046008
  Edges = 1 edges r=1: [Edge33]
FEATURE [Part::Chamfer] Chamfer009008030
  Base = -> Chamfer009008029
  Edges = 23 edges r=0.4: [Edge1,Edge2,Edge4,Edge7,Edge8,Edge9,Edge10,Edge11,Edge16,Edge20,Edge21,Edge23,Edge46,Edge47,Edge48,Edge53,Edge62,Edge64,Edge65,Edge66,Edge67,Edge87,Edge88]
FEATURE [Part::MultiFuse] Fusion010020009007006003  label="probe-mount-rev2"
  Shapes = -> [Chamfer009008030,Chamfer009008027]
FEATURE [Part::Feature] Fusion010020009007006003001  label="probe-mount-rev2-rf"
  shape: bbox 31.23 x 20 x 23.5 mm, 72 faces (baked)
FEATURE [Part::MultiFuse] Fusion010020009007006003002
  Shapes = -> [Fusion010020009007006003001,Fusion010020009007006002]
FEATURE [Part::Feature] Part__Feature012003  label="Body"
  shape: bbox 26.66 x 16.68 x 36.75 mm, 74 faces (baked)
FEATURE [Part::Feature] Part__Feature012004  label="Pin"
  shape: bbox 2.652 x 2.652 x 32.75 mm, 7 faces (baked)
FEATURE [App::Part] BLTouch_v3  label="BLTouch v3"
  Group = -> [Part__Feature012003,Part__Feature012004]
  Origin = -> Origin004
FEATURE [Part::MultiFuse] Fusion010020009007006003003  label="bl-touch"
  Placement = pos=(0,-34,36.75) rot=(0,0,1;0rad)
  Shapes = -> [Part__Feature012003,Part__Feature012004]
FEATURE [App::DocumentObjectGroup] Group  label="Preference"
  Group = -> [Part__Feature018,Part__Feature017,Part__Feature013,Part__Feature014,Part__Feature016,lower_4020_fan_duct,Cut007002001001,Cut007002001007,Cylinder005,Common,Part__Feature020,turbo_fan_35x18_2_,Cut007002001002005001,Fusion010020009002,BLTouch_v3,Fusion010020009007006003003]
FEATURE [Part::Feature] Fusion010020009007006003004  label="probe-mount-rev003"
  shape: bbox 31.23 x 20 x 23.5 mm, 72 faces (baked)
FEATURE [Part::Box] Box025014024  label="Cube066"
  AttacherType = Attacher::AttachEngine3D
  Height = 11
  Length = 6
  Placement = pos=(7,-33.9,9) rot=(0,0,1;0rad)
  Width = 5
FEATURE [Part::Box] Box025014025  label="Cube067"
  AttacherType = Attacher::AttachEngine3D
  Height = 11
  Length = 26
  Placement = pos=(1,-33.9,27.5) rot=(0,0,1;0rad)
  Width = 5
FEATURE [Part::Box] Box025014026  label="Cube068"
  AttacherType = Attacher::AttachEngine3D
  Height = 7.5
  Length = 3.5
  Placement = pos=(7,-33.9,20) rot=(0,0,1;0rad)
  Width = 5
FEATURE [Part::Box] Box025014027  label="Cube069"
  AttacherType = Attacher::AttachEngine3D
  Height = 1
  Length = 4.5
  Placement = pos=(7,-33.9,26.5) rot=(0,0,1;0rad)
  Width = 5
FEATURE [Part::Feature] Cut007002001007029003046009  label="fan-duct-rev-2-refined001"
  shape: bbox 52.67 x 64.46 x 26 mm, 198 faces (baked)
FEATURE [Part::Cut] Cut007002001007029003046010
  Base = -> Fusion010020009007006003004
  Tool = -> Box025014025
FEATURE [Part::MultiFuse] Fusion010020009007006003005
  Shapes = -> [Box025014024,Box025014027,Cut007002001007029003046010,Box025014026,Cut007002001007029003046009]
FEATURE [Part::Box] Box025014028  label="Cube070"
  AttacherType = Attacher::AttachEngine3D
  Height = 10
  Length = 10
  Placement = pos=(-3.77,-35.5,26.5) rot=(0,0,1;0rad)
  Width = 10
FEATURE [Part::Chamfer] Chamfer009008031
  Base = -> Box025014028
  Edges = 1 edges r=1: [Edge8]
FEATURE [Part::Cut] Cut007002001007029003046011
  Base = -> Fusion010020009007006003005
  Tool = -> Chamfer009008031
FEATURE [Part::Cylinder] Cylinder029
  Angle = 360
  AttacherType = Attacher::AttachEngine3D
  Height = 6.5
  Placement = pos=(19,-31.4,21) rot=(0,0,1;0rad)
  Radius = 1
FEATURE [Part::Feature] Fusion010020009007003001  label="fan-support001"
  shape: bbox 14 x 22 x 2.8 mm, 26 faces (baked)
FEATURE [Part::Box] Box025014029  label="Cube071"
  AttacherType = Attacher::AttachEngine3D
  Height = 5.2
  Length = 5.2
  Placement = pos=(7.9,-33.9,1.5) rot=(0,0,1;0rad)
  Width = 5
FEATURE [Part::Chamfer] Chamfer009008032
  Base = -> Box025014029
  Edges = 1 edges r=5.1: [Edge4]
  Placement = pos=(0,0,2.3) rot=(0,0,1;0rad)
FEATURE [Part::MultiFuse] Fusion010020009007006003006  label="duct-probe-combined-rev-2"
  Shapes = -> [Cylinder029,Cut007002001007029003046011,Chamfer009008032]
FEATURE [Part::Feature] Cut007002001007029003046001001  label="fan-duct-rev-2-refined002"
  shape: bbox 52.67 x 64.46 x 26 mm, 198 faces (baked)
FEATURE [Part::Box] Box025014031  label="Cube072"
  AttacherType = Attacher::AttachEngine3D
  Height = 3
  Length = 12
  Placement = pos=(-6,-13,0) rot=(0,0,1;0rad)
  Width = 26
FEATURE [Part::Cylinder] Cylinder030
  Angle = 360
  AttacherType = Attacher::AttachEngine3D
  Height = 10
  Radius = 2
FEATURE [Part::Cylinder] Cylinder031
  Angle = 360
  AttacherType = Attacher::AttachEngine3D
  Height = 10
  Placement = pos=(0,9,0) rot=(0,0,1;0rad)
  Radius = 1.6
FEATURE [Part::Cylinder] Cylinder032
  Angle = 360
  AttacherType = Attacher::AttachEngine3D
  Height = 10
  Placement = pos=(0,-9,0) rot=(0,0,1;0rad)
  Radius = 1.6
FEATURE [Part::MultiFuse] Fusion010020009007006003006003
  Shapes = -> [Cylinder031,Cylinder030,Cylinder032]
FEATURE [Part::Cut] Cut007002001007029003046001002
  Base = -> Box025014031
  Placement = pos=(0,-44.9,45) rot=(0,0,1;0rad)
  Tool = -> Fusion010020009007006003006003
FEATURE [Part::Feature] Part__Feature012005001  label="Body002"
  shape: bbox 26.66 x 16.68 x 36.75 mm, 74 faces (baked)
FEATURE [Part::Feature] Part__Feature012006001  label="Pin002"
  shape: bbox 2.652 x 2.652 x 32.75 mm, 7 faces (baked)
FEATURE [Part::MultiFuse] Fusion010020009007006003006004  label="bltouch"
  Placement = pos=(1.08579,-43.7796,0) rot=(0,0,1;1.91986rad)
  Shapes = -> [Part__Feature012005001,Part__Feature012006001]
FEATURE [Part::Feature] Fusion010020009007006003006004001  label="bltouch001"
  Placement = pos=(-1,-3,45.7) rot=(0,0,1;0rad)
  shape: bbox 17.53 x 25.05 x 42.75 mm, 81 faces, 2 solids (baked)
FEATURE [Part::Box] Box025014032  label="Cube073"
  AttacherType = Attacher::AttachEngine3D
  Height = 35
  Length = 17.5
  Placement = pos=(-7,-33.9,16.5) rot=(0,0,1;0rad)
  Width = 5
FEATURE [Part::Box] Box025014033  label="Cube074"
  AttacherType = Attacher::AttachEngine3D
  Height = 5
  Length = 17.5
  Placement = pos=(-7,-59.9,46) rot=(0,0,1;0rad)
  Width = 26
FEATURE [Part::Feature] Fusion010020009007006003006004002001  label="Fusion010020009007006003006004003"
  Placement = pos=(-0.25,0,4) rot=(0,0,1;0rad)
  shape: bbox 9.356 x 20.11 x 10 mm, 9 faces, 3 solids (baked)
FEATURE [Part::Box] Box025014034  label="Cube075"
  AttacherType = Attacher::AttachEngine3D
  Height = 24.25
  Length = 24.25
  Placement = pos=(10.5,-33.9,26.75) rot=(0,0,1;0rad)
  Width = 5
FEATURE [Part::Chamfer] Chamfer009008033
  Base = -> Box025014034
  Edges = 2 edges r=20: [Edge4,Edge6]
  Placement = pos=(-4.25,0,0) rot=(0,0,1;0rad)
FEATURE [Part::Box] Box025014035  label="Cube076"
  AttacherType = Attacher::AttachEngine3D
  Height = 5
  Length = 5
  Placement = pos=(10.25,-33.9,26.75) rot=(0,0,1;0rad)
  Width = 5
FEATURE [Part::Box] Box025014036  label="Cube077"
  AttacherType = Attacher::AttachEngine3D
  Height = 7
  Length = 9.5
  Placement = pos=(26,-33.9,25) rot=(0,0,1;0rad)
  Width = 5
FEATURE [Part::Chamfer] Chamfer009008034
  Base = -> Box025014036
  Edges = 1 edges r=6: [Edge6]
FEATURE [Part::MultiFuse] Fusion010020009007006003006004002002
  Placement = pos=(0,0,-1.75) rot=(0,0,1;0rad)
  Shapes = -> [Chamfer009008033,Chamfer009008034]
FEATURE [Part::Chamfer] Chamfer009008035
  Base = -> Box025014035
  Edges = 1 edges r=4.25: [Edge6]
  Placement = pos=(-0.5,0,0) rot=(0,0,1;0rad)
FEATURE [Part::Chamfer] Chamfer009008036
  Base = -> Box025014033
  Edges = 1 edges: [Edge1 r1=11 r2=8]
FEATURE [Part::Chamfer] Chamfer009008037
  Base = -> Chamfer009008036
  Edges = 1 edges r=5: [Edge15]
FEATURE [Part::Box] Box025014037  label="Cube078"
  AttacherType = Attacher::AttachEngine3D
  Height = 10
  Length = 9
  Placement = pos=(5.5,-38.9,43) rot=(0,0,1;0rad)
  Width = 5
FEATURE [Part::Cut] Cut007002001007029003046001003
  Base = -> Chamfer009008037
  Tool = -> Fusion010020009007006003006004002001
FEATURE [Part::Cut] Cut007002001007029003046001004
  Base = -> Cut007002001007029003046001003
  Tool = -> Box025014037
FEATURE [Part::Chamfer] Chamfer009008038
  Base = -> Box025014032
  Edges = 1 edges r=17.23: [Edge4]
FEATURE [Part::Chamfer] Chamfer009008039
  Base = -> Cut007002001007029003046001004
  Edges = 1 edges r=1: [Edge24]
FEATURE [Part::Chamfer] Chamfer009008040
  Base = -> Chamfer009008039
  Edges = 1 edges r=3: [Edge26]
  Placement = pos=(0,0,-1.75) rot=(0,0,1;0rad)
FEATURE [Part::Box] Box025014039  label="Cube080"
  AttacherType = Attacher::AttachEngine3D
  Height = 10
  Length = 10
  Placement = pos=(-4,-53.5,-5.3) rot=(0,0,1;0rad)
  Width = 10
FEATURE [Part::Cut] Cut007002001007029003046001005  label="bltouch-pos"
  Base = -> Fusion010020009007006003006004001
  Placement = pos=(0,0,-1.75) rot=(0,0,1;0rad)
  Tool = -> Box025014039
FEATURE [Part::Box] Box025014040  label="Cube081"
  AttacherType = Attacher::AttachEngine3D
  Height = 10
  Length = 22
  Placement = pos=(-10,-37,49.25) rot=(0,0,1;0rad)
  Width = 10
FEATURE [Part::Cut] Cut007002001007029003046001006
  Base = -> Chamfer009008038
  Tool = -> Box025014040
FEATURE [Part::MultiFuse] Fusion010020009007006003006004002003  label="duct-with-bltouch-rev1"
  Shapes = -> [Cut007002001007029003046001001,Cut007002001007029003046001006,Chamfer009008040,Fusion010020009007006003006004002002,Chamfer009008035]
FEATURE [Part::Feature] Part__Feature041  label="5015-nozzle_fan"
  Placement = pos=(9.575,-34,37.1) rot=(0,0,1;1.5708rad)
  shape: bbox 52.65 x 15 x 52.12 mm, 76 faces (baked)
FEATURE [Part::Feature] Fusion010020009007006003006004002003001  label="duct-with-bltouch-rev002"
  shape: bbox 58.23 x 70.76 x 47.75 mm, 252 faces (baked)
FEATURE [Part::Feature] Fusion010020009007006003006001  label="duct-probe-combined-rev-003"
  shape: bbox 59.23 x 64.46 x 26 mm, 260 faces (baked)
FEATURE [Part::MultiFuse] Fusion010020009007006003006002  label="duct-probe-combined-rev-2-w-support"
  Shapes = -> [Fusion010020009007006003006001,Fusion010020009007003001]
FEATURE [Part::Box] Box025014041  label="Cube082"
  AttacherType = Attacher::AttachEngine3D
  Height = 10
  Length = 10
  Width = 10
FEATURE [Part::Cut] Cut007002001007012
  Base = -> Cut007002001007011
  Tool = -> Body002004002
FEATURE [Part::Feature] Body002004001  label="inner001"
  Placement = pos=(0,0,0.8) rot=(0,0,1;0rad)
  shape: bbox 34.69 x 36.6 x 8.2 mm, 8 faces (baked)
FEATURE [Part::Feature] Body002003001  label="outer001"
  shape: bbox 37.79 x 39.3 x 10 mm, 10 faces (baked)
FEATURE [Part::Cut] Cut007002001007010
  Base = -> Body002003001
  Tool = -> Body002004001
FEATURE [Part::Feature] Part__Feature050  label="nozzle_fan_duct"
  Placement = pos=(19.577,-10.928,3.3) rot=(0,0,1;0rad)
  shape: bbox 46.01 x 38.99 x 18.01 mm, 128 faces (baked)
FEATURE [Part::Box] Box025014042  label="Cube083"
  AttacherType = Attacher::AttachEngine3D
  Height = 29
  Length = 13
  Placement = pos=(-5.45,-49.5,0) rot=(0,0,1;0rad)
  Width = 49
FEATURE [Part::Cut] Cut007002001007029003046001007
  Base = -> Part__Feature050
  Tool = -> Box025014042
FEATURE [Part::Box] Box025014043  label="Cube084"
  AttacherType = Attacher::AttachEngine3D
  Height = 23
  Length = 16
  Placement = pos=(30.98,-56,0) rot=(0,0,1;0rad)
  Width = 47
FEATURE [Part::Cut] Cut007002001007029003046001008
  Base = -> Cut007002001007029003046001007
  Tool = -> Box025014043
FEATURE [Part::Box] Box025014044  label="Cube085"
  AttacherType = Attacher::AttachEngine3D
  Height = 31
  Length = 35
  Placement = pos=(0,-32.63,0) rot=(0,0,1;0rad)
  Width = 33
FEATURE [Part::Box] Box025014045  label="Cube086"
  AttacherType = Attacher::AttachEngine3D
  Height = 31
  Length = 35
  Placement = pos=(0,-52.34,15.8) rot=(0,0,1;0rad)
  Width = 33
FEATURE [Part::Cut] Cut007002001007029003046001009
  Base = -> Cut007002001007029003046001008
  Tool = -> Box025014044
FEATURE [Part::Box] Box025014046  label="Cube087"
  AttacherType = Attacher::AttachEngine3D
  Height = 31
  Length = 35
  Placement = pos=(0,-52.34,-19.2) rot=(0,0,1;0rad)
  Width = 33
FEATURE [Part::Box] Box025014047  label="Cube088"
  AttacherType = Attacher::AttachEngine3D
  Height = 4
  Length = 1.88
  Placement = pos=(7.55,-50.4321,11.8) rot=(0,0,1;0rad)
  Width = 8.1
FEATURE [Part::Cut] Cut007002001007029003046001010
  Base = -> Cut007002001007029003046001009
  Tool = -> Box025014046
FEATURE [Part::Cut] Cut007002001007029003046001011
  Base = -> Cut007002001007029003046001010
  Tool = -> Box025014045
FEATURE [Part::Box] Box025014048  label="Cube089"
  AttacherType = Attacher::AttachEngine3D
  Height = 2.7
  Length = 1.25
  Placement = pos=(29.73,-50.4321,11.8) rot=(0,0,1;0rad)
  Width = 21.53
FEATURE [Part::Box] Box025014049  label="Cube090"
  AttacherType = Attacher::AttachEngine3D
  Height = 0.7
  Length = 1.88
  Placement = pos=(7.55,-45.4321,11.8) rot=(0,0,1;0rad)
  Width = 9.53
FEATURE [Part::Box] Box025014050  label="Cube091"
  AttacherType = Attacher::AttachEngine3D
  Height = 4
  Length = 1.88
  Placement = pos=(7.55,-50.4321,11.8) rot=(0,0,1;0rad)
  Width = 6.53
FEATURE [Part::Box] Box025014051  label="Cube092"
  AttacherType = Attacher::AttachEngine3D
  Height = 4
  Length = 1.88
  Placement = pos=(7.55,-39.1321,11.8) rot=(0,0,1;0rad)
  Width = 10.23
FEATURE [Part::Box] Box025014052  label="Cube093"
  AttacherType = Attacher::AttachEngine3D
  Height = 4
  Length = 23
  Placement = pos=(7.55,-50.43,11.8) rot=(0,0,1;0rad)
  Width = 1.25
FEATURE [Part::Box] Box025014053  label="Cube094"
  AttacherType = Attacher::AttachEngine3D
  Height = 8
  Length = 32
  Placement = pos=(7.55,-33.9,11.8) rot=(0,0,1;0rad)
  Width = 5
FEATURE [Part::MultiFuse] Fusion010020009007006003006004002003002
  Shapes = -> [Box025014047,Box025014051,Box025014048,Box025014050,Cut007002001007029003046001011,Box025014052,Box025014049,Box025014053,Chamfer009007]
